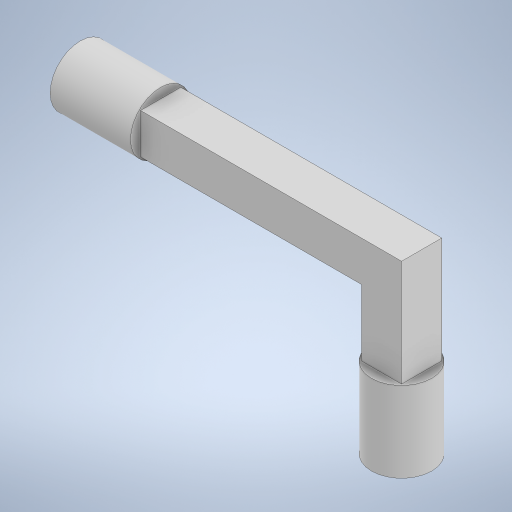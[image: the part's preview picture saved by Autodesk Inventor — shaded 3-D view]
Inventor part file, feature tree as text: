
AUTODESK INVENTOR PART (.ipt)
format: ipt  version: 2024.3 (Build 283343000, 343)  size: 247,296 bytes
history: native  units: mm
features: extrude x3, sketch x3, other x1
ambient origin geometry x8: Origin, YZ Plane, XZ Plane, XY Plane, X Axis, Y Axis, Z Axis, Center Point
bodies: Body1 (feature_tree)
feature tree (7):
  other  "ソリッド1"
  extrude  "押し出し1"  Depth=85.0mm
  extrude  "押し出し2"  Depth=46.5mm
  extrude  "押し出し3"  Depth=10.0mm
  sketch  "スケッチ1"
  sketch  "スケッチ2"
  sketch  "スケッチ3"
